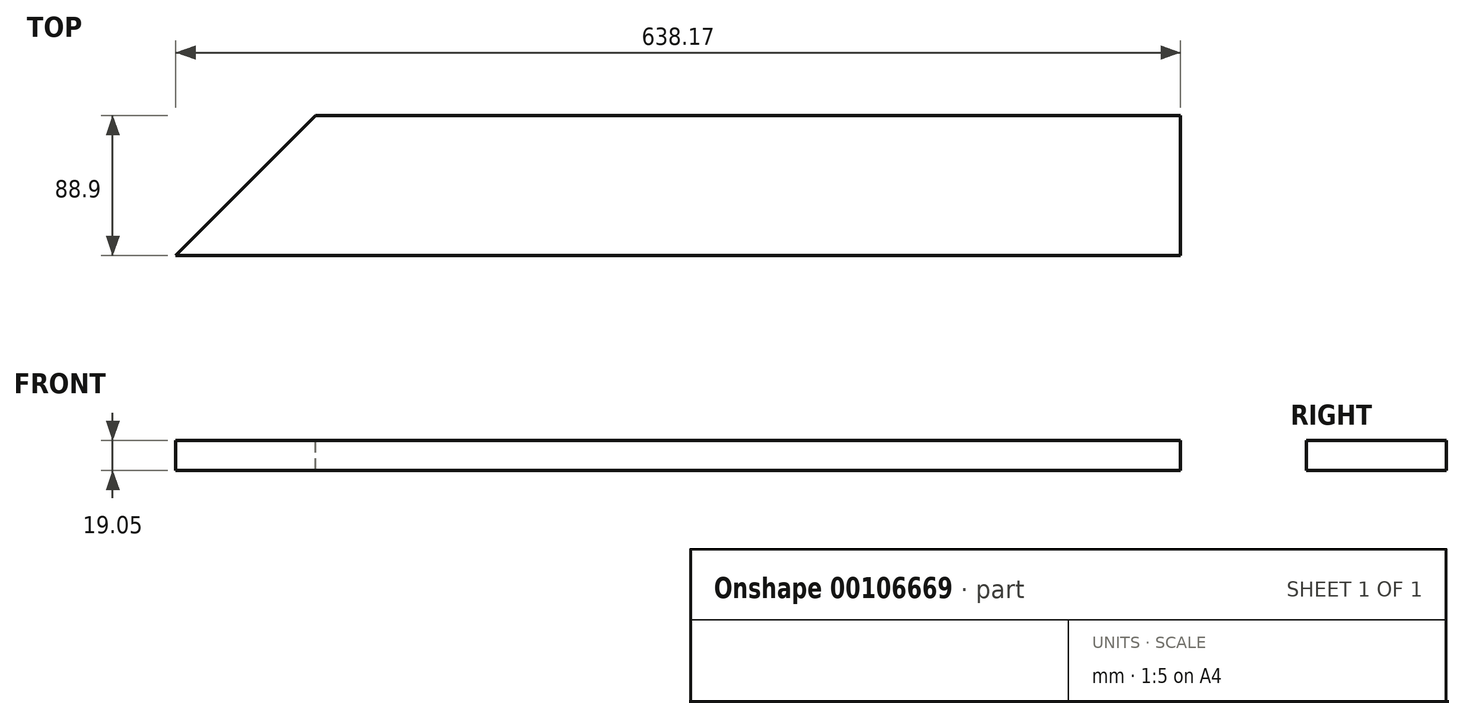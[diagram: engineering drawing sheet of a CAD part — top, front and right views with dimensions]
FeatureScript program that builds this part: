
annotation { "Feature Type Name" : "Feature", "Feature Type Description" : "" }
export const myFeature = defineFeature(function(context is Context, id is Id, definition is map)
    precondition{}
    {
        {
            var Q0;
            Q0=qCreatedBy(makeId("Front.planeOp"),FACE);
            var sketch = newSketch(context, id + "F0", { "sketchPlane" : qUnion([Q0])});
            skLineSegment(sketch, "E0.bottom", {"start": v(1.52, 0) * mm, "end": v(639.7, 0) * mm});
            skLineSegment(sketch, "E0.top", {"start": v(1.52, 19.05) * mm, "end": v(639.7, 19.05) * mm});
            skLineSegment(sketch, "E0.left", {"start": v(1.52, 0) * mm, "end": v(1.52, 19.05) * mm});
            skLineSegment(sketch, "E1", {"start": v(639.7, 19.05) * mm, "end": v(639.7, 0) * mm});
            skSolve(sketch);
        }
        {
            var Q0;
            Q0=makeQuery(id+"F0.imprint","IMPRINT",FACE,{"disambiguationData":[TD([[makeQuery(id+"F0.imprint","IMPRINT",EDGE,{"derivedFrom":sQuery(id+"F0.wireOp",EDGE,"E0.bottom")}),1.0]])]});
            extrude(context, id + "F1", {"entities" : qUnion([Q0]), "depth" : 88.9 * mm});
        }
        {
            var Q0;
            Q0=makeQuery(id+"F1.opExtrude","SWEPT_FACE",FACE,{"disambiguationData":[OSD([sQuery(id+"F0.wireOp",EDGE,"E0.top")])]});
            var sketch = newSketch(context, id + "F2", { "sketchPlane" : qUnion([Q0])});
            skLineSegment(sketch, "E2", {"start": v(1.52, -88.9) * mm, "end": v(90.42, 0) * mm});
            skPoint(sketch, "E3.orphan", {"position": v(0, 121.62) * mm});
            skLineSegment(sketch, "E4", {"start": v(1.52, -88.9) * mm, "end": v(1.52, 0) * mm});
            skLineSegment(sketch, "E5", {"start": v(1.52, 0) * mm, "end": v(90.42, 0) * mm});
            skSolve(sketch);
        }
        {
            var Q0;
            Q0=makeQuery(id+"F2.imprint","IMPRINT",FACE,{"disambiguationData":[TD([[makeQuery(id+"F2.imprint","IMPRINT",EDGE,{"derivedFrom":sQuery(id+"F2.wireOp",EDGE,"E2")}),1.0]])]});
            extrude(context, id + "F3", {"entities" : qUnion([Q0]), "operationType" : NewBodyOperationType.REMOVE, "endBound" : BoundingType.THROUGH_ALL, "oppositeDirection" : true, "depth" : 25.4 * mm});
        }
    });
